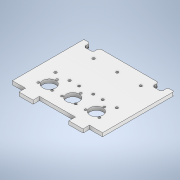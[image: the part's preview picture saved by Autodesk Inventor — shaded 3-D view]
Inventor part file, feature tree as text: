
AUTODESK INVENTOR PART (.ipt)
format: ipt  version: 2020 (Build 240168000, 168)  size: 219,136 bytes
history: native  units: mm
features: extrude x4, sketch x4, pattern_linear x3
ambient origin geometry x8: Origin, YZ Plane, XZ Plane, XY Plane, X Axis, Y Axis, Z Axis, Center Point
bodies: Solid1 (feature_tree)
feature tree (11):
  extrude  "base"  Depth=3.0mm
  extrude  "Poke Hole"  Depth=3.0mm
  pattern_linear  "Rectangular Pattern1"  Spacing1=9.0mm  [1 undecoded]
  extrude  "Mount Holes"  Depth=19.7mm
  pattern_linear  "Rectangular Pattern2"  Spacing1=1.5mm  [1 undecoded]
  extrude  "PCB mount holes"  Depth=126.0mm
  pattern_linear  "Rectangular Pattern3"  Spacing1=18.25mm  [1 undecoded]
  sketch  "Sketch1"  dims[d3=12.7mm d5=3.0mm]
  sketch  "Sketch2"  dims[d7=12.7mm d9=3.0mm]
  sketch  "Sketch3"  dims[d10=9.0mm]
  sketch  "Sketch4"  dims[d11=19.7mm d13=9.0mm d14=19.7mm d16=1.5mm d17=126.0mm d20=18.25mm d21=18.25mm d22=57.15mm d23=9.0mm d24=9.0mm d27=91.0mm d28=91.0mm d29=5.0mm d30=0.0mm d31=18.0mm d32=21.5mm d33=5.0mm d34=0.0mm d35=20.0mm d37=33.0mm d38=20.0mm d40=33.0mm d41=3.0mm d42=11.1mm d43=30.0mm d45=360.0deg d47=5.0mm d48=0.0mm d49=30.0mm d51=33.0mm d52=33.0mm d53=83.0mm d54=3.7mm d55=3.3mm d56=3.3mm d57=19.75mm d58=3.3mm d59=44.5mm d61=7.5mm d62=10.0mm d63=0.0mm d64=30.0mm d66=33.0mm]
note: 3 required parameter values undecoded (feature->parameter linkage not recoverable at this tier; creation-order binding heuristic only, values carry confidence <= 0.55)
